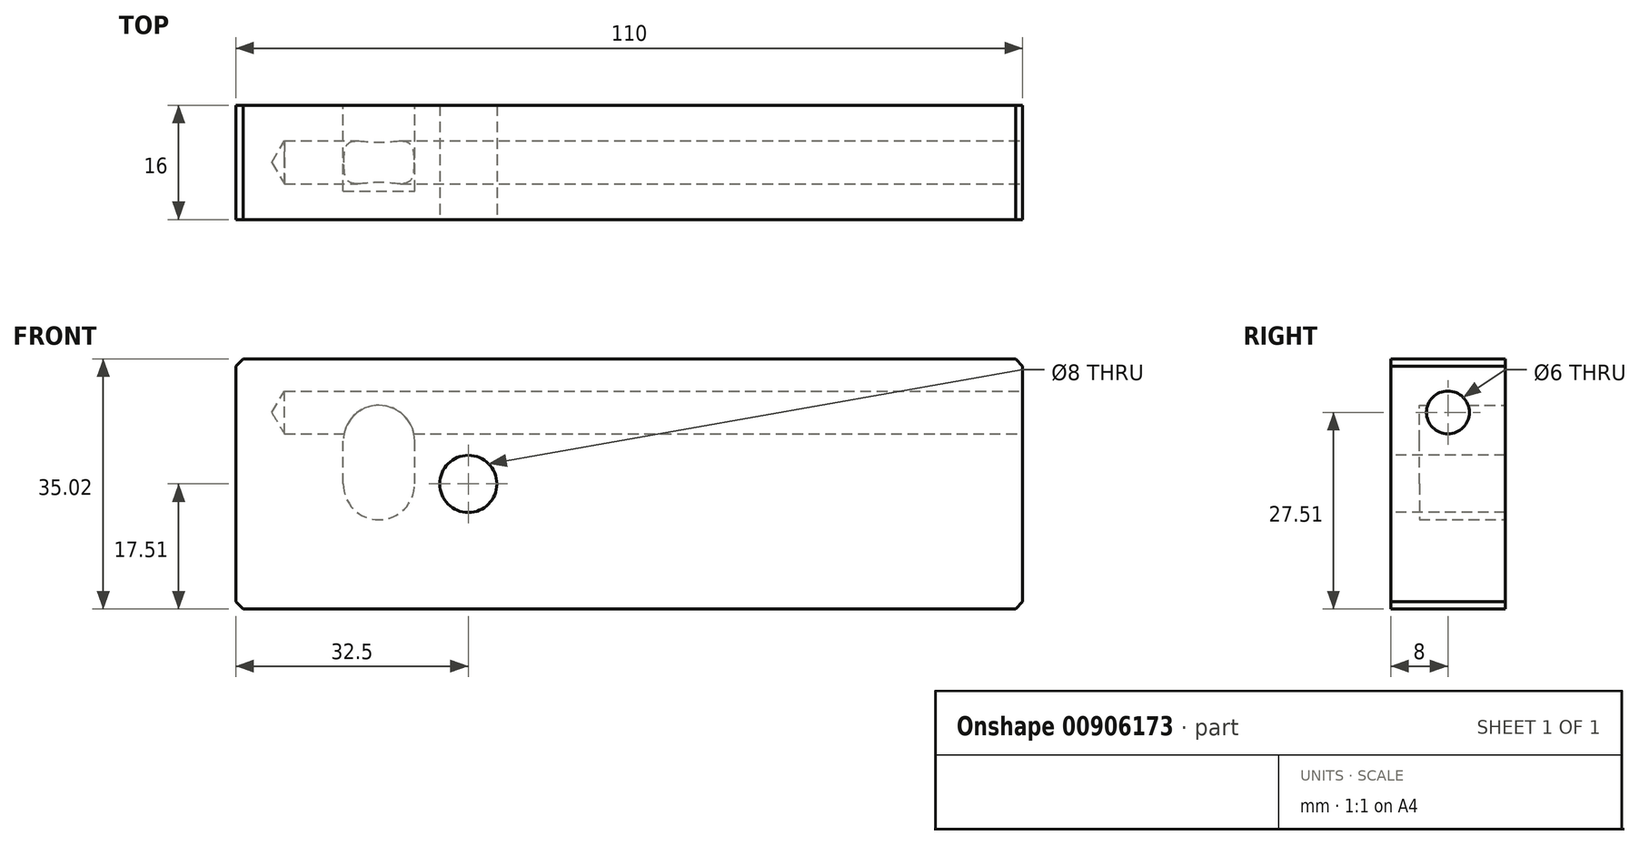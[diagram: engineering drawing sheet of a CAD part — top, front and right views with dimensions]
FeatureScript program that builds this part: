
annotation { "Feature Type Name" : "Feature", "Feature Type Description" : "" }
export const myFeature = defineFeature(function(context is Context, id is Id, definition is map)
    precondition{}
    {
        {
            var Q0;
            Q0=qCreatedBy(makeId("Top.planeOp"),FACE);
            cPlane(context, id + "F0", {"entities" : qUnion([Q0]), "cplaneType" : CPlaneType.OFFSET, "offset" : 10 * mm, "width" : 150 * mm, "height" : 150 * mm});
        }
        {
            var Q0;
            Q0=qCreatedBy(makeId("Front.planeOp"),FACE);
            var sketch = newSketch(context, id + "F1", { "sketchPlane" : qUnion([Q0])});
            skLineSegment(sketch, "E0.bottom", {"start": v(-55, -17.5) * mm, "end": v(55, -17.5) * mm});
            skLineSegment(sketch, "E0.top", {"start": v(-55, 17.5) * mm, "end": v(55, 17.5) * mm});
            skLineSegment(sketch, "E0.left", {"start": v(-55, -17.5) * mm, "end": v(-55, 17.5) * mm});
            skLineSegment(sketch, "E0.right", {"start": v(55, -17.5) * mm, "end": v(55, 17.5) * mm});
            skPoint(sketch, "E0.middle", {"position": v(0, 0) * mm});
            skCircle(sketch, "E1", {"center": v(-22.5, 0) * mm, "radius": 4 * mm});
            skCircle(sketch, "E2", {"center": v(22.5, 0) * mm, "radius": 4 * mm});
            skLineSegment(sketch, "E3", {"start": v(-22.5, 0) * mm, "end": v(0, 0) * mm});
            skLineSegment(sketch, "E4", {"start": v(22.5, 0) * mm, "end": v(0, 0) * mm});
            skCircle(sketch, "E5", {"center": v(-35, 0) * mm, "radius": 5 * mm});
            skCircle(sketch, "E6", {"center": v(35, 0) * mm, "radius": 5 * mm});
            skLineSegment(sketch, "E7", {"start": v(-35, 0) * mm, "end": v(0, 0) * mm});
            skLineSegment(sketch, "E8", {"start": v(35, 0) * mm, "end": v(0, 0) * mm});
            skLineSegment(sketch, "E9.bottom", {"start": v(-45, -17.5) * mm, "end": v(45, -17.5) * mm});
            skLineSegment(sketch, "E9.top", {"start": v(-45, 17.5) * mm, "end": v(45, 17.5) * mm});
            skLineSegment(sketch, "E9.left", {"start": v(-45, -17.5) * mm, "end": v(-45, 17.5) * mm});
            skLineSegment(sketch, "E9.right", {"start": v(45, -17.5) * mm, "end": v(45, 17.5) * mm});
            skSolve(sketch);
        }
        {
            var Q0;
            {var subQ0=sQuery(id+"F1.wireOp",EDGE,"E0.left");Q0=makeQuery(id+"F1.imprint","IMPRINT",FACE,{"disambiguationData":[TD([[makeQuery(id+"F1.imprint","IMPRINT",EDGE,{"derivedFrom":subQ0}),-1.0]])]});}
            var Q1;
            Q1=makeQuery(id+"F1.imprint","IMPRINT",FACE,{"disambiguationData":[TD([[makeQuery(id+"F1.imprint","IMPRINT",EDGE,{"derivedFrom":sQuery(id+"F1.wireOp",EDGE,"E5")}),-1.0]])]});
            var Q2;
            Q2=makeQuery(id+"F1.imprint","IMPRINT",FACE,{"disambiguationData":[TD([[makeQuery(id+"F1.imprint","IMPRINT",EDGE,{"derivedFrom":sQuery(id+"F1.wireOp",EDGE,"E5")}),1.0]])]});
            var Q3;
            {var subQ0=sQuery(id+"F1.wireOp",EDGE,"E7");var subQ4=makeQuery(id+"F1.imprint","IMPRINT",VERTEX,{"derivedFrom":subQ0});Q3=makeQuery(id+"F1.imprint","IMPRINT",FACE,{"disambiguationData":[TD([[makeQuery(id+"F1.imprint","IMPRINT",EDGE,{"disambiguationData":[TD([[subQ4,1.0]])],"derivedFrom":subQ0}),-1.0]])]});}
            var Q4;
            {var subQ0=sQuery(id+"F1.wireOp",EDGE,"E7");var subQ4=makeQuery(id+"F1.imprint","IMPRINT",VERTEX,{"derivedFrom":subQ0});Q4=makeQuery(id+"F1.imprint","IMPRINT",FACE,{"disambiguationData":[TD([[makeQuery(id+"F1.imprint","IMPRINT",EDGE,{"disambiguationData":[TD([[subQ4,1.0]])],"derivedFrom":subQ0}),1.0]])]});}
            var Q5;
            {var subQ0=sQuery(id+"F1.wireOp",EDGE,"E8");var subQ4=makeQuery(id+"F1.imprint","IMPRINT",VERTEX,{"derivedFrom":subQ0});Q5=makeQuery(id+"F1.imprint","IMPRINT",FACE,{"disambiguationData":[TD([[makeQuery(id+"F1.imprint","IMPRINT",EDGE,{"disambiguationData":[TD([[subQ4,1.0]])],"derivedFrom":subQ0}),1.0]])]});}
            var Q6;
            {var subQ0=sQuery(id+"F1.wireOp",EDGE,"E8");var subQ4=makeQuery(id+"F1.imprint","IMPRINT",VERTEX,{"derivedFrom":subQ0});Q6=makeQuery(id+"F1.imprint","IMPRINT",FACE,{"disambiguationData":[TD([[makeQuery(id+"F1.imprint","IMPRINT",EDGE,{"disambiguationData":[TD([[subQ4,1.0]])],"derivedFrom":subQ0}),-1.0]])]});}
            var Q7;
            Q7=makeQuery(id+"F1.imprint","IMPRINT",FACE,{"disambiguationData":[TD([[makeQuery(id+"F1.imprint","IMPRINT",EDGE,{"derivedFrom":sQuery(id+"F1.wireOp",EDGE,"E6")}),1.0]])]});
            var Q8;
            {var subQ0=sQuery(id+"F1.wireOp",EDGE,"E0.right");Q8=makeQuery(id+"F1.imprint","IMPRINT",FACE,{"disambiguationData":[TD([[makeQuery(id+"F1.imprint","IMPRINT",EDGE,{"derivedFrom":subQ0}),1.0]])]});}
            extrude(context, id + "F2", {"entities" : qUnion([Q0, Q1, Q2, Q3, Q4, Q5, Q6, Q7, Q8]), "oppositeDirection" : true, "depth" : 16 * mm, "offsetDistance" : 25 * mm});
        }
        {
            var Q0;
            Q0=makeQuery(id+"F2.opExtrude","SWEPT_EDGE",EDGE,{"disambiguationData":[OSD([sQuery(id+"F1.wireOp",EDGE,"E0.bottom"),sQuery(id+"F1.wireOp",EDGE,"E0.right")])]});
            var Q1;
            Q1=makeQuery(id+"F2.opExtrude","SWEPT_EDGE",EDGE,{"disambiguationData":[OSD([sQuery(id+"F1.wireOp",EDGE,"E0.top"),sQuery(id+"F1.wireOp",EDGE,"E0.right")])]});
            var Q2;
            Q2=makeQuery(id+"F2.opExtrude","SWEPT_EDGE",EDGE,{"disambiguationData":[OSD([sQuery(id+"F1.wireOp",EDGE,"E0.bottom"),sQuery(id+"F1.wireOp",EDGE,"E0.left")])]});
            var Q3;
            Q3=makeQuery(id+"F2.opExtrude","SWEPT_EDGE",EDGE,{"disambiguationData":[OSD([sQuery(id+"F1.wireOp",EDGE,"E0.top"),sQuery(id+"F1.wireOp",EDGE,"E0.left")])]});
            var Q4;
            Q4=makeQuery(id+"F2.opExtrude","SWEPT_EDGE",EDGE,{"disambiguationData":[OSD([sQuery(id+"F1.wireOp",EDGE,"E0.bottom"),sQuery(id+"F1.wireOp",EDGE,"E9.bottom"),sQuery(id+"F1.wireOp",EDGE,"E9.right")])]});
            var Q5;
            Q5=makeQuery(id+"F2.opExtrude","SWEPT_EDGE",EDGE,{"disambiguationData":[OSD([sQuery(id+"F1.wireOp",EDGE,"E0.top"),sQuery(id+"F1.wireOp",EDGE,"E9.top"),sQuery(id+"F1.wireOp",EDGE,"E9.right")])]});
            chamfer(context, id + "F3", {"entities" : qUnion([Q0, Q1, Q2, Q3, Q4, Q5]), "width" : 1 * mm, "tangentPropagation" : true});
        }
        {
            var Q0;
            Q0=qCreatedBy(id+"F0.planeOp",FACE);
            var sketch = newSketch(context, id + "F4", { "sketchPlane" : qUnion([Q0])});
            skLineSegment(sketch, "E10", {"start": v(57.66, 8) * mm, "end": v(-50, 8) * mm});
            skLineSegment(sketch, "E11", {"start": v(57.66, 5) * mm, "end": v(-48.2, 5) * mm});
            skLineSegment(sketch, "E12", {"start": v(-48.2, 5) * mm, "end": v(-50, 8) * mm});
            skLineSegment(sketch, "E13", {"start": v(57.66, 5) * mm, "end": v(57.66, 8) * mm});
            skSolve(sketch);
        }
        {
            var Q0;
            Q0=makeQuery(id+"F4.imprint","IMPRINT",FACE,{"disambiguationData":[TD([[makeQuery(id+"F4.imprint","IMPRINT",EDGE,{"derivedFrom":sQuery(id+"F4.wireOp",EDGE,"E10")}),1.0]])]});
            var Q1;
            Q1=sQuery(id+"F4.wireOp",EDGE,"E13");
            var Q2;
            Q2=sQuery(id+"F4.wireOp",EDGE,"E11");
            var Q3;
            Q3=sQuery(id+"F4.wireOp",EDGE,"E12");
            var Q4;
            Q4=sQuery(id+"F4.wireOp",EDGE,"E10");
            var Q5;
            Q5=sQuery(id+"F4.wireOp",EDGE,"E10");
            revolve(context, id + "F5", {"operationType" : NewBodyOperationType.REMOVE, "surfaceOperationType" : NewSurfaceOperationType.NEW, "entities" : qUnion([Q0]), "surfaceEntities" : qUnion([Q1, Q2, Q3, Q4]), "axis" : qUnion([Q5]), "revolveType" : RevolveType.FULL});
        }
        {
            var Q0;
            Q0=makeQuery(id+"F2.opExtrude","CAP_FACE",FACE,{"disambiguationData":[OSD([sQuery(id+"F1.wireOp",EDGE,"E0.bottom"),sQuery(id+"F1.wireOp",EDGE,"E0.top"),sQuery(id+"F1.wireOp",EDGE,"E0.left"),sQuery(id+"F1.wireOp",EDGE,"E9.bottom"),sQuery(id+"F1.wireOp",EDGE,"E9.top"),sQuery(id+"F1.wireOp",EDGE,"E9.right")])],"isStart":false});
            var sketch = newSketch(context, id + "F6", { "sketchPlane" : qUnion([Q0])});
            skArc(sketch, "E14", {"start": v(30, 0) * mm, "mid": v(35, -5) * mm, "end": v(40, 0) * mm});
            skArc(sketch, "E15", {"start": v(40, 6) * mm, "mid": v(35, 11) * mm, "end": v(30, 6) * mm});
            skLineSegment(sketch, "E16", {"start": v(40, 0) * mm, "end": v(40, 6) * mm});
            skLineSegment(sketch, "E17", {"start": v(30, 0) * mm, "end": v(30, 6) * mm});
            skSolve(sketch);
        }
        {
            var Q0;
            Q0 = qSketchRegion(id + "F6", true);
            extrude(context, id + "F7", {"entities" : qUnion([Q0]), "operationType" : NewBodyOperationType.REMOVE, "oppositeDirection" : true, "depth" : 12 * mm, "offsetDistance" : 25 * mm});
        }
        {
            var Q0;
            {var subQ0=sQuery(id+"F1.wireOp",EDGE,"E7");var subQ4=makeQuery(id+"F1.imprint","IMPRINT",VERTEX,{"derivedFrom":subQ0});Q0=makeQuery(id+"F1.imprint","IMPRINT",FACE,{"disambiguationData":[TD([[makeQuery(id+"F1.imprint","IMPRINT",EDGE,{"disambiguationData":[TD([[subQ4,1.0]])],"derivedFrom":subQ0}),-1.0]])]});}
            var Q1;
            {var subQ0=sQuery(id+"F1.wireOp",EDGE,"E7");var subQ4=makeQuery(id+"F1.imprint","IMPRINT",VERTEX,{"derivedFrom":subQ0});Q1=makeQuery(id+"F1.imprint","IMPRINT",FACE,{"disambiguationData":[TD([[makeQuery(id+"F1.imprint","IMPRINT",EDGE,{"disambiguationData":[TD([[subQ4,1.0]])],"derivedFrom":subQ0}),1.0]])]});}
            extrude(context, id + "F8", {"entities" : qUnion([Q0, Q1]), "operationType" : NewBodyOperationType.REMOVE, "oppositeDirection" : true, "depth" : 25 * mm, "offsetDistance" : 25 * mm});
        }
    });
